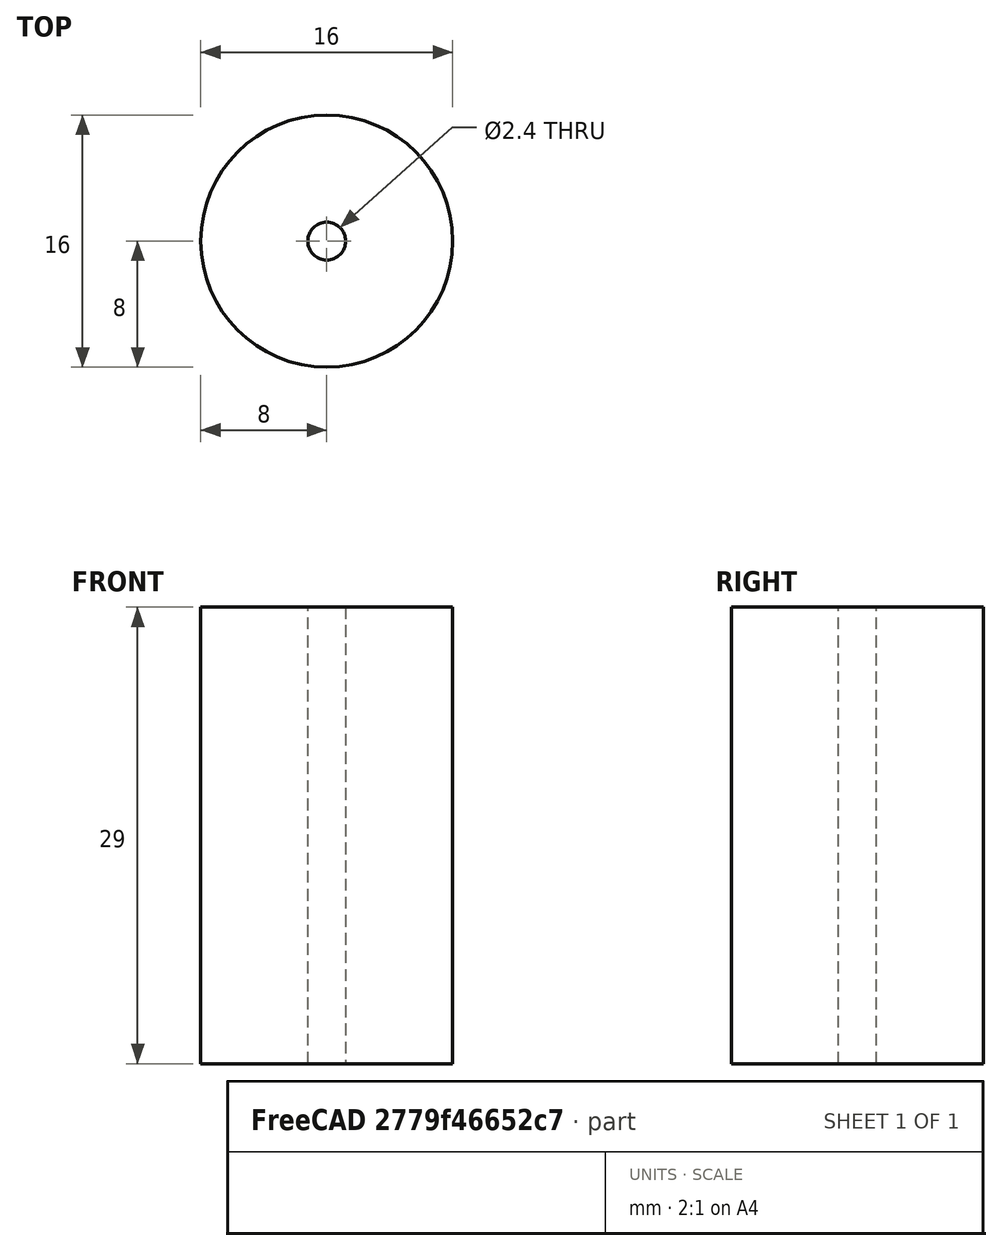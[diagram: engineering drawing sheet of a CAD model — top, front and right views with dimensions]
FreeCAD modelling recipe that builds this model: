
FCSTD DOCUMENT  (FreeCAD 0.21R33668 +26 (Git))
Label: board_connector_top_mid
License: All rights reserved
LicenseURL: https://en.wikipedia.org/wiki/All_rights_reserved
objects: Sketcher::SketchObject×2, PartDesign::Pad×1, PartDesign::Pocket×1, PartDesign::Body×1
note: 7 computed .brp shape members not serialized (recipe doc carries the construction recipe); baked Part::Feature solids carry a one-line shape summary decoded from their .brp

FEATURE [Sketcher::SketchObject] Sketch
  FullyConstrained = false
  MapMode = 5
  Support = -> [XY_Plane]
  sketch-geometry (2):
    g0: Circle CenterX=0 CenterY=0 CenterZ=0 NormalX=0 NormalY=0 NormalZ=1 AngleXU=0 Radius=8
    g1: GeomPoint X=-5.04833 Y=6.206 Z=0
  constraints (3):
    c: Coincident(g0,g-1)
    c: PointOnObject(g1,g0)
    c: Distance(g1,g0) = 8
FEATURE [PartDesign::Pad] Pad
  Direction = (0,0,1)
  Length = 29
  Length2 = 10
  Profile = -> Sketch
  ReferenceAxis = -> Sketch [N_Axis]
  Type = 0
FEATURE [Sketcher::SketchObject] Sketch001
  FullyConstrained = false
  MapMode = 5
  Placement = pos=(0,0,29) rot=(0,0,1;0rad)
  Support = -> [Pad]
  sketch-geometry (2):
    g0: Circle CenterX=0 CenterY=0 CenterZ=0 NormalX=0 NormalY=0 NormalZ=1 AngleXU=0 Radius=1.2
    g1: GeomPoint X=-0.940143 Y=0.745742 Z=0
  constraints (3):
    c: Coincident(g0,g-1)
    c: PointOnObject(g1,g0)
    c: Distance(g1,g0) = 1.2
FEATURE [PartDesign::Pocket] Pocket
  BaseFeature = -> Pad
  Direction = (0,0,-1)
  Length = 31
  Length2 = 5
  Profile = -> Sketch001
  ReferenceAxis = -> Sketch001 [N_Axis]
  Type = 0
FEATURE [PartDesign::Body] Body
  Group = -> [Sketch,Pad,Sketch001,Pocket]
  Origin = -> Origin
  Tip = -> Pocket
